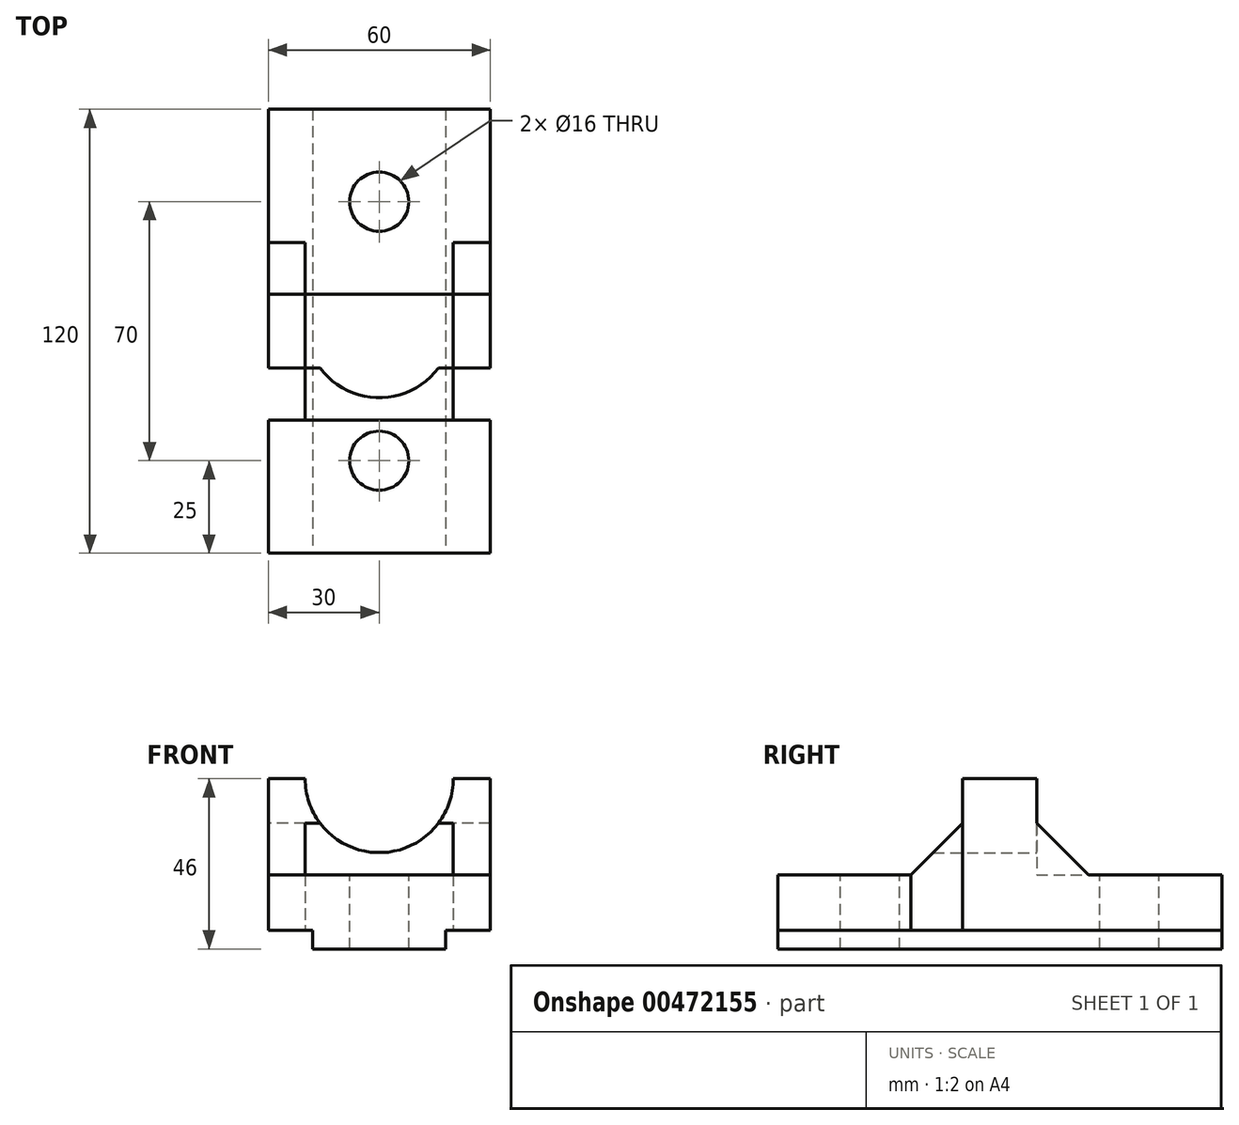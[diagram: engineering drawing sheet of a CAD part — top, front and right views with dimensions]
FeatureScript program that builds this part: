
annotation { "Feature Type Name" : "Feature", "Feature Type Description" : "" }
export const myFeature = defineFeature(function(context is Context, id is Id, definition is map)
    precondition{}
    {
        {
            var Q0;
            Q0=qCreatedBy(makeId("Top.planeOp"),FACE);
            var sketch = newSketch(context, id + "F0", { "sketchPlane" : qUnion([Q0])});
            skLineSegment(sketch, "E0.bottom", {"start": v(30, 60) * mm, "end": v(-30, 60) * mm});
            skLineSegment(sketch, "E0.top", {"start": v(30, -60) * mm, "end": v(-30, -60) * mm});
            skLineSegment(sketch, "E0.left", {"start": v(30, 60) * mm, "end": v(30, -60) * mm});
            skLineSegment(sketch, "E0.right", {"start": v(-30, 60) * mm, "end": v(-30, -60) * mm});
            skPoint(sketch, "E0.middle", {"position": v(0, 0) * mm});
            skSolve(sketch);
        }
        {
            var Q0;
            Q0 = qSketchRegion(id + "F0", true);
            extrude(context, id + "F1", {"entities" : qUnion([Q0]), "depth" : 20 * mm});
        }
        {
            var Q0;
            Q0=makeQuery(id+"F1.opExtrude","SWEPT_FACE",FACE,{"disambiguationData":[OSD([sQuery(id+"F0.wireOp",EDGE,"E0.top")])]});
            var sketch = newSketch(context, id + "F2", { "sketchPlane" : qUnion([Q0])});
            skLineSegment(sketch, "E1.bottom", {"start": v(-30, 0) * mm, "end": v(-18, 0) * mm});
            skLineSegment(sketch, "E1.top", {"start": v(-30, 5) * mm, "end": v(-18, 5) * mm});
            skLineSegment(sketch, "E1.left", {"start": v(-30, 0) * mm, "end": v(-30, 5) * mm});
            skLineSegment(sketch, "E1.right", {"start": v(-18, 0) * mm, "end": v(-18, 5) * mm});
            skLineSegment(sketch, "E2.bottom", {"start": v(30, 0) * mm, "end": v(18, 0) * mm});
            skLineSegment(sketch, "E2.top", {"start": v(30, 5) * mm, "end": v(18, 5) * mm});
            skLineSegment(sketch, "E2.left", {"start": v(30, 0) * mm, "end": v(30, 5) * mm});
            skLineSegment(sketch, "E2.right", {"start": v(18, 0) * mm, "end": v(18, 5) * mm});
            skSolve(sketch);
        }
        {
            var Q0;
            Q0 = qSketchRegion(id + "F2", true);
            extrude(context, id + "F3", {"entities" : qUnion([Q0]), "operationType" : NewBodyOperationType.REMOVE, "oppositeDirection" : true, "depth" : 258.3 * mm});
        }
        {
            var Q0;
            Q0=qCreatedBy(makeId("Right.planeOp"),FACE);
            var sketch = newSketch(context, id + "F4", { "sketchPlane" : qUnion([Q0])});
            skLineSegment(sketch, "E3.0.0", {"start": v(-60, 5) * mm, "end": v(60, 5) * mm});
            skLineSegment(sketch, "E3.0.1", {"start": v(60, 5) * mm, "end": v(60, 20) * mm});
            skLineSegment(sketch, "E3.0.2", {"start": v(60, 20) * mm, "end": v(-60, 20) * mm});
            skLineSegment(sketch, "E3.0.3", {"start": v(-60, 20) * mm, "end": v(-60, 5) * mm});
            skLineSegment(sketch, "E4.0.0", {"start": v(60, 0) * mm, "end": v(60, 5) * mm});
            skLineSegment(sketch, "E4.0.1", {"start": v(60, 5) * mm, "end": v(-60, 5) * mm});
            skLineSegment(sketch, "E4.0.2", {"start": v(-60, 5) * mm, "end": v(-60, 0) * mm});
            skLineSegment(sketch, "E4.0.3", {"start": v(-60, 0) * mm, "end": v(60, 0) * mm});
            skLineSegment(sketch, "E5", {"start": v(0, 0) * mm, "end": v(0, 46) * mm});
            skLineSegment(sketch, "E6", {"start": v(0, 46) * mm, "end": v(-10, 46) * mm});
            skLineSegment(sketch, "E7", {"start": v(-10, 46) * mm, "end": v(10, 46) * mm});
            skLineSegment(sketch, "E8", {"start": v(10, 46) * mm, "end": v(10, 34) * mm});
            skLineSegment(sketch, "E9", {"start": v(10, 34) * mm, "end": v(24, 20) * mm});
            skLineSegment(sketch, "E10.MirrorCS", {"start": v(10, 46) * mm, "end": v(-10, 46) * mm});
            skLineSegment(sketch, "E11.MirrorCS", {"start": v(-10, 46) * mm, "end": v(-10, 34) * mm});
            skLineSegment(sketch, "E12.MirrorCS", {"start": v(-10, 34) * mm, "end": v(-24, 20) * mm});
            skSolve(sketch);
        }
        {
            var Q0;
            {var subQ1=sQuery(id+"F4.wireOp",EDGE,"E8");Q0=makeQuery(id+"F4.imprint","IMPRINT",FACE,{"disambiguationData":[TD([[makeQuery(id+"F4.imprint","IMPRINT",EDGE,{"derivedFrom":subQ1}),-1.0]])]});}
            var Q1;
            {var subQ0=sQuery(id+"F4.wireOp",EDGE,"E11.MirrorCS");Q1=makeQuery(id+"F4.imprint","IMPRINT",FACE,{"disambiguationData":[TD([[makeQuery(id+"F4.imprint","IMPRINT",EDGE,{"derivedFrom":subQ0}),1.0]])]});}
            extrude(context, id + "F5", {"entities" : qUnion([Q0, Q1]), "operationType" : NewBodyOperationType.ADD, "depth" : 30 * mm, "hasSecondDirection" : true, "secondDirectionOppositeDirection" : true, "secondDirectionDepth" : 30 * mm});
        }
        {
            var Q0;
            Q0=makeQuery(id+"F5.opExtrude","SWEPT_FACE",FACE,{"disambiguationData":[OSD([sQuery(id+"F4.wireOp",EDGE,"E8")])]});
            var sketch = newSketch(context, id + "F6", { "sketchPlane" : qUnion([Q0])});
            skCircle(sketch, "E13", {"center": v(0, 46) * mm, "radius": 20 * mm});
            skSolve(sketch);
        }
        {
            var Q0;
            Q0 = qSketchRegion(id + "F6", true);
            extrude(context, id + "F7", {"entities" : qUnion([Q0]), "operationType" : NewBodyOperationType.REMOVE, "oppositeDirection" : true, "depth" : 64 * mm, "hasSecondDirection" : true, "secondDirectionOppositeDirection" : false, "secondDirectionDepth" : 66 * mm});
        }
        {
            var Q0;
            {var subQ0=sQuery(id+"F0.wireOp",EDGE,"E0.right");var subQ1=sQuery(id+"F0.wireOp",EDGE,"E0.left");var subQ8=sQuery(id+"F0.wireOp",EDGE,"E0.top");Q0=makeQuery(id+"F5.boolean.opBoolean","SPLIT",FACE,{"disambiguationData":[TD([makeQuery(id+"F1.opExtrude","SWEPT_FACE",FACE,{"disambiguationData":[OSD([subQ8])]})])],"derivedFrom":makeQuery(id+"F1.opExtrude","CAP_FACE",FACE,{"disambiguationData":[OSD([sQuery(id+"F0.wireOp",EDGE,"E0.bottom"),subQ8,subQ1,subQ0])],"isStart":false})});}
            var sketch = newSketch(context, id + "F8", { "sketchPlane" : qUnion([Q0])});
            skLineSegment(sketch, "E14", {"start": v(0, -60) * mm, "end": v(0, -35) * mm});
            skPoint(sketch, "E14.endSnap0", {"position": v(0, -60) * mm});
            skCircle(sketch, "E15", {"center": v(0, -35) * mm, "radius": 8 * mm});
            skCircle(sketch, "E16.MirrorC", {"center": v(0, 35) * mm, "radius": 8 * mm});
            skSolve(sketch);
        }
        {
            var Q0;
            Q0 = qSketchRegion(id + "F8", true);
            extrude(context, id + "F9", {"entities" : qUnion([Q0]), "operationType" : NewBodyOperationType.REMOVE, "oppositeDirection" : true, "depth" : 44.3 * mm});
        }
        {
            var Q0;
            Q0=qCreatedBy(makeId("Top.planeOp"),FACE);
            var sketch = newSketch(context, id + "F10", { "sketchPlane" : qUnion([Q0])});
            skLineSegment(sketch, "E17.0.2", {"start": v(-16, -10) * mm, "end": v(-30, -10) * mm});
            skLineSegment(sketch, "E17.0.3", {"start": v(-30, -10) * mm, "end": v(-30, -24) * mm});
            skLineSegment(sketch, "E17.0.4", {"start": v(-30, -24) * mm, "end": v(30, -24) * mm});
            skLineSegment(sketch, "E18.0.0", {"start": v(-30, -10) * mm, "end": v(-16, -10) * mm});
            skLineSegment(sketch, "E18.0.1", {"start": v(-16, -10) * mm, "end": v(-20, -10) * mm});
            skLineSegment(sketch, "E18.0.2", {"start": v(-20, -10) * mm, "end": v(-30, -10) * mm});
            skPoint(sketch, "E18.1", {"position": v(-25, -10) * mm});
            skPoint(sketch, "E19.0", {"position": v(-18.97, -10) * mm});
            skLineSegment(sketch, "E20", {"start": v(-20, -10) * mm, "end": v(-20, -24) * mm});
            skLineSegment(sketch, "E21", {"start": v(-20, -24) * mm, "end": v(-30, -24) * mm});
            skLineSegment(sketch, "E22", {"start": v(16, -24) * mm, "end": v(30, -24) * mm});
            skLineSegment(sketch, "E23", {"start": v(30, -24) * mm, "end": v(30, -10) * mm});
            skLineSegment(sketch, "E24", {"start": v(30, -10) * mm, "end": v(20, -10) * mm});
            skLineSegment(sketch, "E25", {"start": v(20, -10) * mm, "end": v(20, -24) * mm});
            skLineSegment(sketch, "E26", {"start": v(-20, -10) * mm, "end": v(20, -10) * mm});
            skSolve(sketch);
        }
        {
            var Q0;
            {var subQ2=sQuery(id+"F10.wireOp",EDGE,"E17.0.4");Q0=makeQuery(id+"F10.imprint","IMPRINT",FACE,{"disambiguationData":[TD([[makeQuery(id+"F10.imprint","IMPRINT",EDGE,{"derivedFrom":subQ2}),1.0]])]});}
            extrude(context, id + "F11", {"entities" : qUnion([Q0]), "operationType" : NewBodyOperationType.REMOVE, "depth" : 115 * mm});
        }
        {
            var Q0;
            Q0=qCreatedBy(makeId("Top.planeOp"),FACE);
            var sketch = newSketch(context, id + "F12", { "sketchPlane" : qUnion([Q0])});
            skLineSegment(sketch, "E27.0.1", {"start": v(20, 10) * mm, "end": v(30, 10) * mm});
            skLineSegment(sketch, "E27.0.2", {"start": v(30, 10) * mm, "end": v(30, 24) * mm});
            skLineSegment(sketch, "E27.0.3", {"start": v(30, 24) * mm, "end": v(-30, 24) * mm});
            skLineSegment(sketch, "E27.0.4", {"start": v(-30, 24) * mm, "end": v(-30, 10) * mm});
            skLineSegment(sketch, "E27.0.5", {"start": v(-30, 10) * mm, "end": v(-20, 10) * mm});
            skLineSegment(sketch, "E28", {"start": v(-20, 10) * mm, "end": v(-20, 24) * mm});
            skLineSegment(sketch, "E29", {"start": v(30, 10) * mm, "end": v(20, 10) * mm});
            skLineSegment(sketch, "E30", {"start": v(20, 10) * mm, "end": v(20, 24) * mm});
            skPoint(sketch, "E31.orphan", {"position": v(-16, 10) * mm});
            skPoint(sketch, "E32.orphan", {"position": v(16, 10) * mm});
            skLineSegment(sketch, "E33", {"start": v(-20, 10) * mm, "end": v(20, 10) * mm});
            skSolve(sketch);
        }
        {
            var Q0;
            {var subQ0=sQuery(id+"F12.wireOp",EDGE,"E28");Q0=makeQuery(id+"F12.imprint","IMPRINT",FACE,{"disambiguationData":[TD([[makeQuery(id+"F12.imprint","IMPRINT",EDGE,{"derivedFrom":subQ0}),-1.0]])]});}
            extrude(context, id + "F13", {"entities" : qUnion([Q0]), "operationType" : NewBodyOperationType.REMOVE, "depth" : 57 * mm});
        }
        {
            var Q0;
            Q0=makeQuery(id+"F13.boolean.opBoolean","COPY",FACE,{"derivedFrom":makeQuery(id+"F13.opExtrude","SWEPT_FACE",FACE,{"disambiguationData":[OSD([sQuery(id+"F12.wireOp",EDGE,"E27.0.3")])]})});
            extrude(context, id + "F14", {"entities" : qUnion([Q0]), "operationType" : NewBodyOperationType.ADD, "depth" : 49 * mm});
        }
    });
